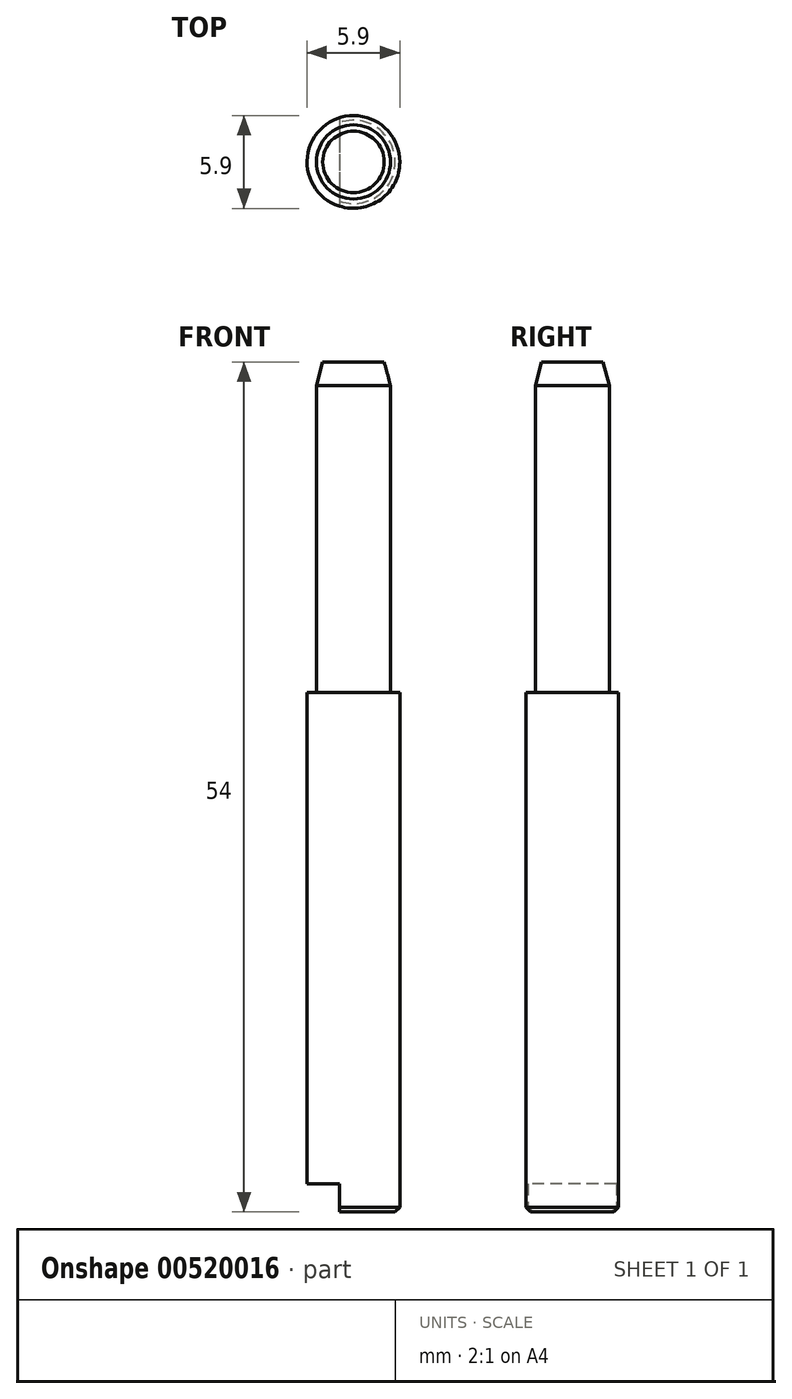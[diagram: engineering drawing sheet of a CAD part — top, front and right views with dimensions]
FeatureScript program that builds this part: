
annotation { "Feature Type Name" : "Feature", "Feature Type Description" : "" }
export const myFeature = defineFeature(function(context is Context, id is Id, definition is map)
    precondition{}
    {
        {
            var Q0;
            Q0=qCreatedBy(makeId("Top.planeOp"),FACE);
            var sketch = newSketch(context, id + "F0", { "sketchPlane" : qUnion([Q0])});
            skCircle(sketch, "E0", {"center": v(0, 0) * mm, "radius": 0.98 * mm});
            skSolve(sketch);
        }
        {
            var Q0;
            Q0=qSketchRegion(id+"F0",true);
            extrude(context, id + "F1", {"entities" : qUnion([Q0]), "depth" : 11 * mm});
        }
        {
            var Q0;
            Q0=makeQuery(id+"F1.opExtrude","CAP_FACE",FACE,{"disambiguationData":[OSD([sQuery(id+"F0.wireOp",EDGE,"E0")])],"isStart":false});
            var sketch = newSketch(context, id + "F2", { "sketchPlane" : qUnion([Q0])});
            skCircle(sketch, "E1", {"center": v(0, 0) * mm, "radius": 0.78 * mm});
            skSolve(sketch);
        }
        {
            var Q0;
            Q0=qSketchRegion(id+"F2",true);
            extrude(context, id + "F3", {"entities" : qUnion([Q0]), "operationType" : NewBodyOperationType.ADD, "depth" : 7 * mm});
        }
        {
            var Q0;
            Q0=makeQuery(id+"F1.opExtrude","CAP_EDGE",EDGE,{"disambiguationData":[OSD([sQuery(id+"F0.wireOp",EDGE,"E0")])],"isStart":true});
            chamfer(context, id + "F4", {"entities" : qUnion([Q0]), "width" : 0.1 * mm, "tangentPropagation" : true});
        }
        {
            var Q0;
            Q0=makeQuery(id+"F3.opExtrude","CAP_EDGE",EDGE,{"disambiguationData":[OSD([sQuery(id+"F2.wireOp",EDGE,"E1")])],"isStart":false});
            chamfer(context, id + "F5", {"entities" : qUnion([Q0]), "chamferType" : ChamferType.OFFSET_ANGLE, "width" : 0.5 * mm, "oppositeDirection" : true, "angle" : 15 * degree, "tangentPropagation" : true});
        }
        {
            var Q0;
            Q0=qCreatedBy(makeId("Front.planeOp"),FACE);
            var sketch = newSketch(context, id + "F6", { "sketchPlane" : qUnion([Q0])});
            skLineSegment(sketch, "E2.bottom", {"start": v(-0.3, 0) * mm, "end": v(-1, 0) * mm});
            skLineSegment(sketch, "E2.top", {"start": v(-0.3, 0.6) * mm, "end": v(-1, 0.6) * mm});
            skLineSegment(sketch, "E2.left", {"start": v(-0.3, 0) * mm, "end": v(-0.3, 0.6) * mm});
            skLineSegment(sketch, "E2.right", {"start": v(-1, 0) * mm, "end": v(-1, 0.6) * mm});
            skSolve(sketch);
        }
        {
            var Q0;
            Q0=qSketchRegion(id+"F6",true);
            extrude(context, id + "F7", {"entities" : qUnion([Q0]), "operationType" : NewBodyOperationType.REMOVE, "endBound" : BoundingType.SYMMETRIC, "oppositeDirection" : true, "depth" : 2 * mm});
        }
        {
            var Q0;
            Q0=makeQuery(id+"F1.opExtrude","SWEPT_BODY",BODY,{"disambiguationData":[OSD([sQuery(id+"F0.wireOp",EDGE,"E0")])]});
            var Q1;
            Q1=qCreatedBy(makeId("Origin.pointOp"),VERTEX);
            transform(context, id + "F8", {"entities" : qUnion([Q0]), "transformType" : TransformType.SCALE_UNIFORMLY, "scale" : 3, "makeCopy" : false, "scalePoint" : qUnion([Q1])});
        }
    });
